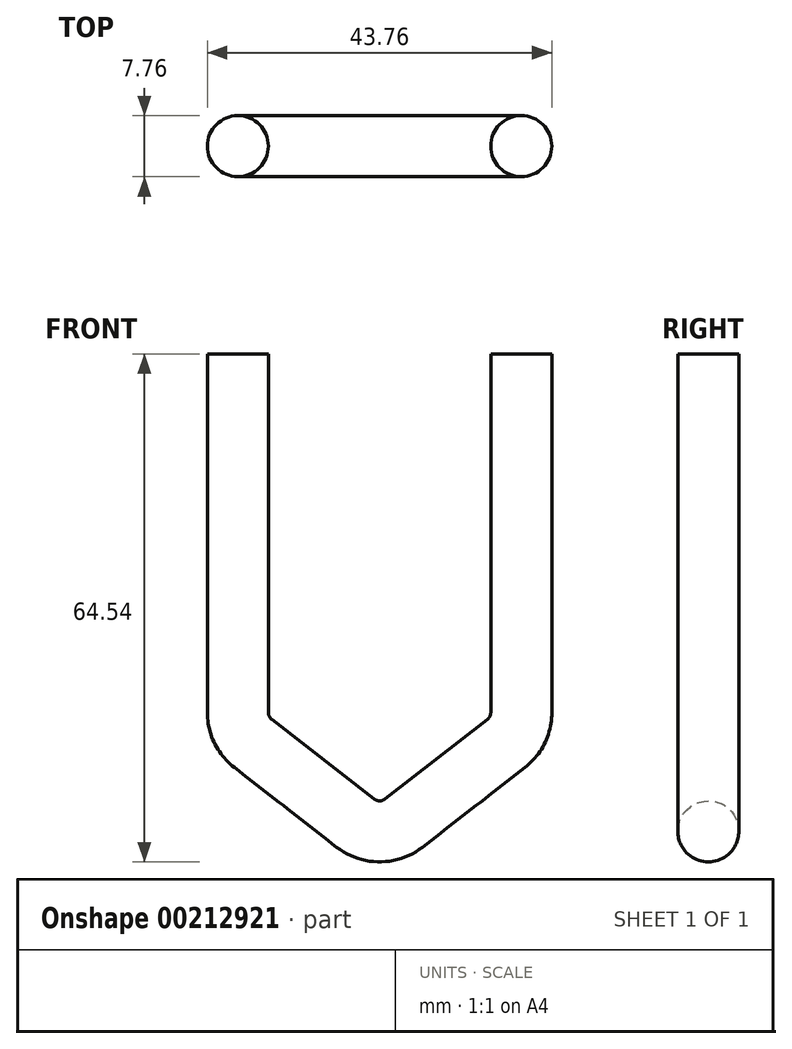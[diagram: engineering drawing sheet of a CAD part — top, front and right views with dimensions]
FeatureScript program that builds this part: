
annotation { "Feature Type Name" : "Feature", "Feature Type Description" : "" }
export const myFeature = defineFeature(function(context is Context, id is Id, definition is map)
    precondition{}
    {
        {
            var Q0;
            Q0=qCreatedBy(makeId("Front.planeOp"),FACE);
            var sketch = newSketch(context, id + "F0", { "sketchPlane" : qUnion([Q0])});
            skLineSegment(sketch, "E0", {"start": v(-3.07, 2.39) * mm, "end": v(-16.07, 12.5) * mm});
            skLineSegment(sketch, "E1", {"start": v(-18, 16.45) * mm, "end": v(-18, 62) * mm});
            skLineSegment(sketch, "E2", {"start": v(3.07, 2.39) * mm, "end": v(16.07, 12.5) * mm});
            skLineSegment(sketch, "E3", {"start": v(18, 16.45) * mm, "end": v(18, 62) * mm});
            skPoint(sketch, "E4.visualSharp", {"position": v(-18, 14) * mm});
            skArc(sketch, "E4.filletArc", {"start": v(-18, 16.45) * mm, "mid": v(-17.5, 14.25) * mm, "end": v(-16.07, 12.5) * mm});
            skPoint(sketch, "E5.visualSharp", {"position": v(0, 0) * mm});
            skArc(sketch, "E5.filletArc", {"start": v(-3.07, 2.39) * mm, "mid": v(0, 1.33) * mm, "end": v(3.07, 2.39) * mm});
            skPoint(sketch, "E6.visualSharp", {"position": v(18, 14) * mm});
            skArc(sketch, "E6.filletArc", {"start": v(16.07, 12.5) * mm, "mid": v(17.5, 14.25) * mm, "end": v(18, 16.45) * mm});
            skSolve(sketch);
        }
        {
            var Q0;
            Q0=qCreatedBy(makeId("Top.planeOp"),FACE);
            cPlane(context, id + "F1", {"entities" : qUnion([Q0]), "cplaneType" : CPlaneType.OFFSET, "offset" : 62 * mm, "width" : 150 * mm, "height" : 150 * mm});
        }
        {
            var Q0;
            Q0=qCreatedBy(id+"F1.planeOp",FACE);
            var sketch = newSketch(context, id + "F2", { "sketchPlane" : qUnion([Q0])});
            skCircle(sketch, "E7", {"center": v(18, 0) * mm, "radius": 3.88 * mm});
            skSolve(sketch);
        }
        {
            var Q0;
            Q0=makeQuery(id+"F2.imprint","IMPRINT",FACE,{"disambiguationData":[TD([[makeQuery(id+"F2.imprint","IMPRINT",EDGE,{"derivedFrom":sQuery(id+"F2.wireOp",EDGE,"E7")}),1.0]])]});
            var Q1;
            Q1=sQuery(id+"F0.wireOp",EDGE,"E3");
            var Q2;
            Q2=sQuery(id+"F0.wireOp",EDGE,"E6.filletArc");
            var Q3;
            Q3=sQuery(id+"F0.wireOp",EDGE,"E2");
            var Q4;
            Q4=sQuery(id+"F0.wireOp",EDGE,"E5.filletArc");
            var Q5;
            Q5=sQuery(id+"F0.wireOp",EDGE,"E0");
            var Q6;
            Q6=sQuery(id+"F0.wireOp",EDGE,"E4.filletArc");
            var Q7;
            Q7=sQuery(id+"F0.wireOp",EDGE,"E1");
            sweep(context, id + "F3", {"profiles" : qUnion([Q0]), "path" : qUnion([Q1, Q2, Q3, Q4, Q5, Q6, Q7])});
        }
    });
